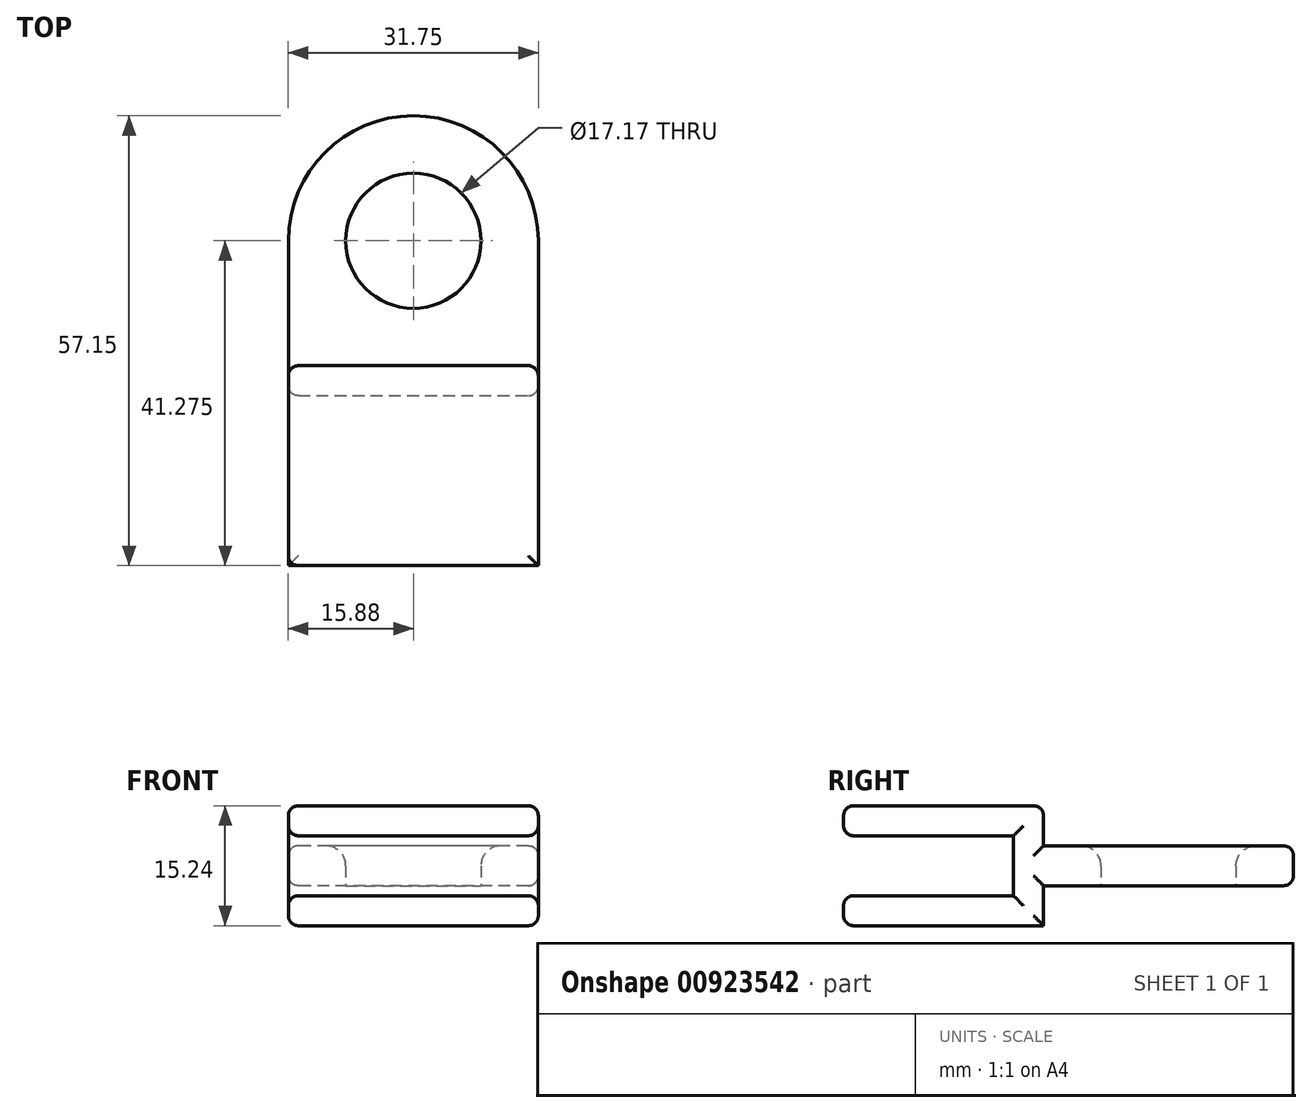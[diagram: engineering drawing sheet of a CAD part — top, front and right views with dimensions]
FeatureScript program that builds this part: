
annotation { "Feature Type Name" : "Feature", "Feature Type Description" : "" }
export const myFeature = defineFeature(function(context is Context, id is Id, definition is map)
    precondition{}
    {
        {
            var Q0;
            Q0=qCreatedBy(makeId("Top.planeOp"),FACE);
            var sketch = newSketch(context, id + "F0", { "sketchPlane" : qUnion([Q0])});
            skLineSegment(sketch, "E0.bottom", {"start": v(-14.05, 14.63) * mm, "end": v(17.7, 14.63) * mm});
            skLineSegment(sketch, "E0.top", {"start": v(-14.05, -10.77) * mm, "end": v(17.7, -10.77) * mm});
            skLineSegment(sketch, "E0.left", {"start": v(-14.05, 14.63) * mm, "end": v(-14.05, -10.77) * mm});
            skLineSegment(sketch, "E0.right", {"start": v(17.7, 14.63) * mm, "end": v(17.7, -10.77) * mm});
            skSolve(sketch);
        }
        {
            var Q0;
            Q0 = qSketchRegion(id + "F0", true);
            extrude(context, id + "F1", {"entities" : qUnion([Q0]), "depth" : 3.8 * mm, "offsetDistance" : 25.4 * mm});
        }
        {
            var Q0;
            Q0=makeQuery(id+"F1.opExtrude","CAP_FACE",FACE,{"disambiguationData":[OSD([sQuery(id+"F0.wireOp",EDGE,"E0.bottom"),sQuery(id+"F0.wireOp",EDGE,"E0.top"),sQuery(id+"F0.wireOp",EDGE,"E0.left"),sQuery(id+"F0.wireOp",EDGE,"E0.right")])],"isStart":false});
            var sketch = newSketch(context, id + "F2", { "sketchPlane" : qUnion([Q0])});
            skLineSegment(sketch, "E1.bottom", {"start": v(-14.05, 14.63) * mm, "end": v(17.7, 14.63) * mm});
            skLineSegment(sketch, "E1.top", {"start": v(-14.05, 10.82) * mm, "end": v(17.7, 10.82) * mm});
            skLineSegment(sketch, "E1.left", {"start": v(-14.05, 14.63) * mm, "end": v(-14.05, 10.82) * mm});
            skLineSegment(sketch, "E1.right", {"start": v(17.7, 14.63) * mm, "end": v(17.7, 10.82) * mm});
            skSolve(sketch);
        }
        {
            var Q0;
            Q0 = qSketchRegion(id + "F2", true);
            extrude(context, id + "F3", {"entities" : qUnion([Q0]), "operationType" : NewBodyOperationType.ADD, "depth" : 3.8 * mm, "offsetDistance" : 25.4 * mm});
        }
        {
            var Q0;
            Q0=makeQuery(id+"F1.opExtrude","SWEPT_BODY",BODY,{"disambiguationData":[OSD([sQuery(id+"F0.wireOp",EDGE,"E0.bottom"),sQuery(id+"F0.wireOp",EDGE,"E0.top"),sQuery(id+"F0.wireOp",EDGE,"E0.left"),sQuery(id+"F0.wireOp",EDGE,"E0.right")])]});
            var Q1;
            Q1=makeQuery(id+"F3.opExtrude","CAP_FACE",FACE,{"disambiguationData":[OSD([sQuery(id+"F2.wireOp",EDGE,"E1.bottom"),sQuery(id+"F2.wireOp",EDGE,"E1.top"),sQuery(id+"F2.wireOp",EDGE,"E1.left"),sQuery(id+"F2.wireOp",EDGE,"E1.right")])],"isStart":false});
            mirror(context, id + "F4", {"operationType" : NewBodyOperationType.ADD, "entities" : qUnion([Q0]), "mirrorPlane" : qUnion([Q1])});
        }
        {
            var Q0;
            {var subQ0=makeQuery(id+"F3.boolean.opBoolean","MERGE",FACE,{"derivedFrom":[makeQuery(id+"F1.opExtrude","SWEPT_FACE",FACE,{"disambiguationData":[OSD([sQuery(id+"F0.wireOp",EDGE,"E0.bottom")])]}),makeQuery(id+"F3.opExtrude","SWEPT_FACE",FACE,{"disambiguationData":[OSD([sQuery(id+"F2.wireOp",EDGE,"E1.bottom")])]})]});Q0=makeQuery(id+"F4.boolean.opBoolean","MERGE",FACE,{"derivedFrom":[subQ0,makeQuery(id+"F4.opPattern","COPY",FACE,{"derivedFrom":subQ0,"instanceName":"1"})]});}
            var sketch = newSketch(context, id + "F5", { "sketchPlane" : qUnion([Q0])});
            skLineSegment(sketch, "E2.bottom", {"start": v(-17.7, 10.16) * mm, "end": v(14.05, 10.16) * mm});
            skLineSegment(sketch, "E2.top", {"start": v(-17.7, 5.08) * mm, "end": v(14.05, 5.08) * mm});
            skLineSegment(sketch, "E2.left", {"start": v(-17.7, 10.16) * mm, "end": v(-17.7, 5.08) * mm});
            skLineSegment(sketch, "E2.right", {"start": v(14.05, 11.43) * mm, "end": v(14.05, 5.08) * mm});
            skSolve(sketch);
        }
        {
            var Q0;
            Q0 = qSketchRegion(id + "F5", true);
            extrude(context, id + "F6", {"entities" : qUnion([Q0]), "operationType" : NewBodyOperationType.ADD, "depth" : 31.75 * mm, "offsetDistance" : 25.4 * mm});
        }
        {
            var Q0;
            Q0=makeQuery(id+"F6.opExtrude","SWEPT_FACE",FACE,{"disambiguationData":[OSD([sQuery(id+"F5.wireOp",EDGE,"E2.top")])]});
            var sketch = newSketch(context, id + "F7", { "sketchPlane" : qUnion([Q0])});
            skCircle(sketch, "E3", {"center": v(1.83, -30.5) * mm, "radius": 8.59 * mm});
            skSolve(sketch);
        }
        {
            var Q0;
            Q0 = qSketchRegion(id + "F7", true);
            extrude(context, id + "F8", {"entities" : qUnion([Q0]), "operationType" : NewBodyOperationType.REMOVE, "endBound" : BoundingType.THROUGH_ALL, "oppositeDirection" : true, "depth" : 25.4 * mm, "offsetDistance" : 25.4 * mm});
        }
        {
            var Q0;
            Q0=makeQuery(id+"F6.opExtrude","CAP_EDGE",EDGE,{"disambiguationData":[OSD([sQuery(id+"F5.wireOp",EDGE,"E2.left")])],"isStart":false});
            fillet(context, id + "F9", {"entities" : qUnion([Q0]), "radius" : 15.88 * mm, "tangentPropagation" : true, "allowEdgeOverflow" : false});
        }
        {
            var Q0;
            Q0=makeQuery(id+"F6.opExtrude","CAP_EDGE",EDGE,{"disambiguationData":[OSD([sQuery(id+"F5.wireOp",EDGE,"E2.right")])],"isStart":false});
            fillet(context, id + "F10", {"entities" : qUnion([Q0]), "radius" : 15.88 * mm, "tangentPropagation" : true, "allowEdgeOverflow" : false});
        }
        {
            var Q0;
            Q0=makeQuery(id+"F4.opPattern","COPY",EDGE,{"derivedFrom":makeQuery(id+"F1.opExtrude","SWEPT_EDGE",EDGE,{"disambiguationData":[OSD([sQuery(id+"F0.wireOp",EDGE,"E0.top"),sQuery(id+"F0.wireOp",EDGE,"E0.left")])]}),"instanceName":"1"});
            var Q1;
            Q1=makeQuery(id+"F4.opPattern","COPY",EDGE,{"derivedFrom":makeQuery(id+"F1.opExtrude","CAP_EDGE",EDGE,{"disambiguationData":[OSD([sQuery(id+"F0.wireOp",EDGE,"E0.left")])],"isStart":false}),"instanceName":"1"});
            var Q2;
            Q2=makeQuery(id+"F4.opPattern","COPY",EDGE,{"derivedFrom":makeQuery(id+"F1.opExtrude","CAP_EDGE",EDGE,{"disambiguationData":[OSD([sQuery(id+"F0.wireOp",EDGE,"E0.left")])],"isStart":true}),"instanceName":"1"});
            var Q3;
            Q3=makeQuery(id+"F1.opExtrude","CAP_EDGE",EDGE,{"disambiguationData":[OSD([sQuery(id+"F0.wireOp",EDGE,"E0.left")])],"isStart":false});
            var Q4;
            Q4=makeQuery(id+"F1.opExtrude","CAP_EDGE",EDGE,{"disambiguationData":[OSD([sQuery(id+"F0.wireOp",EDGE,"E0.left")])],"isStart":true});
            var Q5;
            {var subQ0=makeQuery(id+"F3.opExtrude","SWEPT_EDGE",EDGE,{"disambiguationData":[OSD([sQuery(id+"F0.wireOp",EDGE,"E0.left"),sQuery(id+"F2.wireOp",EDGE,"E1.top"),sQuery(id+"F2.wireOp",EDGE,"E1.left")])]});Q5=makeQuery(id+"F4.boolean.opBoolean","MERGE",EDGE,{"derivedFrom":[subQ0,makeQuery(id+"F4.opPattern","COPY",EDGE,{"derivedFrom":subQ0,"instanceName":"1"})]});}
            var Q6;
            Q6=makeQuery(id+"F6.opExtrude","SWEPT_EDGE",EDGE,{"disambiguationData":[OSD([sQuery(id+"F5.wireOp",EDGE,"E2.bottom"),sQuery(id+"F5.wireOp",EDGE,"E2.right")])]});
            var Q7;
            Q7=makeQuery(id+"F6.opExtrude","SWEPT_EDGE",EDGE,{"disambiguationData":[OSD([sQuery(id+"F0.wireOp",EDGE,"E0.bottom"),sQuery(id+"F0.wireOp",EDGE,"E0.left"),sQuery(id+"F2.wireOp",EDGE,"E1.bottom"),sQuery(id+"F2.wireOp",EDGE,"E1.left"),sQuery(id+"F5.wireOp",EDGE,"E2.top"),sQuery(id+"F5.wireOp",EDGE,"E2.right")])]});
            var Q8;
            Q8=makeQuery(id+"F4.opPattern","COPY",EDGE,{"derivedFrom":makeQuery(id+"F1.opExtrude","CAP_EDGE",EDGE,{"disambiguationData":[OSD([sQuery(id+"F0.wireOp",EDGE,"E0.bottom")])],"isStart":true}),"instanceName":"1"});
            var Q9;
            {var subQ0=sQuery(id+"F2.wireOp",EDGE,"E1.left");var subQ2=sQuery(id+"F2.wireOp",EDGE,"E1.bottom");var subQ4=sQuery(id+"F0.wireOp",EDGE,"E0.left");var subQ6=sQuery(id+"F0.wireOp",EDGE,"E0.bottom");var subQ8=makeQuery(id+"F3.boolean.opBoolean","MERGE",EDGE,{"derivedFrom":[makeQuery(id+"F1.opExtrude","SWEPT_EDGE",EDGE,{"disambiguationData":[OSD([subQ6,subQ4])]}),makeQuery(id+"F3.opExtrude","SWEPT_EDGE",EDGE,{"disambiguationData":[OSD([subQ2,subQ0])]})]});Q9=makeQuery(id+"F6.boolean.opBoolean","SPLIT",EDGE,{"disambiguationData":[TD([makeQuery(id+"F6.opExtrude","SWEPT_FACE",FACE,{"disambiguationData":[OSD([sQuery(id+"F5.wireOp",EDGE,"E2.bottom")])]})])],"derivedFrom":makeQuery(id+"F4.boolean.opBoolean","MERGE",EDGE,{"derivedFrom":[subQ8,makeQuery(id+"F4.opPattern","COPY",EDGE,{"derivedFrom":subQ8,"instanceName":"1"})]})});}
            var Q10;
            {var subQ0=sQuery(id+"F2.wireOp",EDGE,"E1.bottom");var subQ2=sQuery(id+"F0.wireOp",EDGE,"E0.left");var subQ3=sQuery(id+"F0.wireOp",EDGE,"E0.bottom");var subQ6=sQuery(id+"F2.wireOp",EDGE,"E1.left");var subQ8=makeQuery(id+"F3.boolean.opBoolean","MERGE",EDGE,{"derivedFrom":[makeQuery(id+"F1.opExtrude","SWEPT_EDGE",EDGE,{"disambiguationData":[OSD([subQ3,subQ2])]}),makeQuery(id+"F3.opExtrude","SWEPT_EDGE",EDGE,{"disambiguationData":[OSD([subQ0,subQ6])]})]});Q10=makeQuery(id+"F6.boolean.opBoolean","SPLIT",EDGE,{"disambiguationData":[TD([makeQuery(id+"F6.opExtrude","SWEPT_FACE",FACE,{"disambiguationData":[OSD([sQuery(id+"F5.wireOp",EDGE,"E2.top")])]})])],"derivedFrom":makeQuery(id+"F4.boolean.opBoolean","MERGE",EDGE,{"derivedFrom":[subQ8,makeQuery(id+"F4.opPattern","COPY",EDGE,{"derivedFrom":subQ8,"instanceName":"1"})]})});}
            var Q11;
            Q11=makeQuery(id+"F1.opExtrude","CAP_EDGE",EDGE,{"disambiguationData":[OSD([sQuery(id+"F0.wireOp",EDGE,"E0.top")])],"isStart":false});
            var Q12;
            Q12=makeQuery(id+"F4.opPattern","COPY",EDGE,{"derivedFrom":makeQuery(id+"F1.opExtrude","CAP_EDGE",EDGE,{"disambiguationData":[OSD([sQuery(id+"F0.wireOp",EDGE,"E0.top")])],"isStart":false}),"instanceName":"1"});
            var Q13;
            Q13=makeQuery(id+"F1.opExtrude","CAP_EDGE",EDGE,{"disambiguationData":[OSD([sQuery(id+"F0.wireOp",EDGE,"E0.top")])],"isStart":true});
            var Q14;
            Q14=makeQuery(id+"F4.opPattern","COPY",EDGE,{"derivedFrom":makeQuery(id+"F1.opExtrude","CAP_EDGE",EDGE,{"disambiguationData":[OSD([sQuery(id+"F0.wireOp",EDGE,"E0.top")])],"isStart":true}),"instanceName":"1"});
            var Q15;
            Q15=makeQuery(id+"F4.opPattern","COPY",EDGE,{"derivedFrom":makeQuery(id+"F1.opExtrude","CAP_EDGE",EDGE,{"disambiguationData":[OSD([sQuery(id+"F0.wireOp",EDGE,"E0.right")])],"isStart":true}),"instanceName":"1"});
            var Q16;
            Q16=makeQuery(id+"F4.opPattern","COPY",EDGE,{"derivedFrom":makeQuery(id+"F1.opExtrude","CAP_EDGE",EDGE,{"disambiguationData":[OSD([sQuery(id+"F0.wireOp",EDGE,"E0.right")])],"isStart":false}),"instanceName":"1"});
            var Q17;
            Q17=makeQuery(id+"F1.opExtrude","CAP_EDGE",EDGE,{"disambiguationData":[OSD([sQuery(id+"F0.wireOp",EDGE,"E0.right")])],"isStart":false});
            var Q18;
            Q18=makeQuery(id+"F1.opExtrude","CAP_EDGE",EDGE,{"disambiguationData":[OSD([sQuery(id+"F0.wireOp",EDGE,"E0.right")])],"isStart":true});
            var Q19;
            {var subQ0=sQuery(id+"F2.wireOp",EDGE,"E1.bottom");var subQ2=sQuery(id+"F0.wireOp",EDGE,"E0.right");var subQ3=sQuery(id+"F0.wireOp",EDGE,"E0.bottom");var subQ6=sQuery(id+"F2.wireOp",EDGE,"E1.right");var subQ8=makeQuery(id+"F3.boolean.opBoolean","MERGE",EDGE,{"derivedFrom":[makeQuery(id+"F1.opExtrude","SWEPT_EDGE",EDGE,{"disambiguationData":[OSD([subQ3,subQ2])]}),makeQuery(id+"F3.opExtrude","SWEPT_EDGE",EDGE,{"disambiguationData":[OSD([subQ0,subQ6])]})]});Q19=makeQuery(id+"F6.boolean.opBoolean","SPLIT",EDGE,{"disambiguationData":[TD([makeQuery(id+"F6.opExtrude","SWEPT_FACE",FACE,{"disambiguationData":[OSD([sQuery(id+"F5.wireOp",EDGE,"E2.top")])]})])],"derivedFrom":makeQuery(id+"F4.boolean.opBoolean","MERGE",EDGE,{"derivedFrom":[subQ8,makeQuery(id+"F4.opPattern","COPY",EDGE,{"derivedFrom":subQ8,"instanceName":"1"})]})});}
            var Q20;
            {var subQ0=sQuery(id+"F2.wireOp",EDGE,"E1.right");var subQ2=sQuery(id+"F2.wireOp",EDGE,"E1.bottom");var subQ4=sQuery(id+"F0.wireOp",EDGE,"E0.right");var subQ6=sQuery(id+"F0.wireOp",EDGE,"E0.bottom");var subQ8=makeQuery(id+"F3.boolean.opBoolean","MERGE",EDGE,{"derivedFrom":[makeQuery(id+"F1.opExtrude","SWEPT_EDGE",EDGE,{"disambiguationData":[OSD([subQ6,subQ4])]}),makeQuery(id+"F3.opExtrude","SWEPT_EDGE",EDGE,{"disambiguationData":[OSD([subQ2,subQ0])]})]});Q20=makeQuery(id+"F6.boolean.opBoolean","SPLIT",EDGE,{"disambiguationData":[TD([makeQuery(id+"F6.opExtrude","SWEPT_FACE",FACE,{"disambiguationData":[OSD([sQuery(id+"F5.wireOp",EDGE,"E2.bottom")])]})])],"derivedFrom":makeQuery(id+"F4.boolean.opBoolean","MERGE",EDGE,{"derivedFrom":[subQ8,makeQuery(id+"F4.opPattern","COPY",EDGE,{"derivedFrom":subQ8,"instanceName":"1"})]})});}
            var Q21;
            {var subQ0=makeQuery(id+"F3.opExtrude","SWEPT_EDGE",EDGE,{"disambiguationData":[OSD([sQuery(id+"F0.wireOp",EDGE,"E0.right"),sQuery(id+"F2.wireOp",EDGE,"E1.top"),sQuery(id+"F2.wireOp",EDGE,"E1.right")])]});Q21=makeQuery(id+"F4.boolean.opBoolean","MERGE",EDGE,{"derivedFrom":[subQ0,makeQuery(id+"F4.opPattern","COPY",EDGE,{"derivedFrom":subQ0,"instanceName":"1"})]});}
            fillet(context, id + "F11", {"entities" : qUnion([Q0, Q1, Q2, Q3, Q4, Q5, Q6, Q7, Q8, Q9, Q10, Q11, Q12, Q13, Q14, Q15, Q16, Q17, Q18, Q19, Q20, Q21]), "radius" : 1.27 * mm, "tangentPropagation" : true, "allowEdgeOverflow" : false});
        }
        {
            var Q0;
            Q0=makeQuery(id+"F8.boolean.opBoolean","INTERSECT",EDGE,{"derivedFrom":[makeQuery(id+"F6.opExtrude","SWEPT_FACE",FACE,{"disambiguationData":[OSD([sQuery(id+"F5.wireOp",EDGE,"E2.bottom")])]}),makeQuery(id+"F8.opExtrude","SWEPT_FACE",FACE,{"disambiguationData":[OSD([sQuery(id+"F7.wireOp",EDGE,"E3")])]})]});
            var Q1;
            Q1=makeQuery(id+"F8.boolean.opBoolean","COPY",EDGE,{"derivedFrom":makeQuery(id+"F8.opExtrude","CAP_EDGE",EDGE,{"disambiguationData":[OSD([sQuery(id+"F7.wireOp",EDGE,"E3")])],"isStart":true})});
            fillet(context, id + "F12", {"entities" : qUnion([Q0, Q1]), "radius" : 2.54 * mm, "tangentPropagation" : true, "allowEdgeOverflow" : false});
        }
    });
